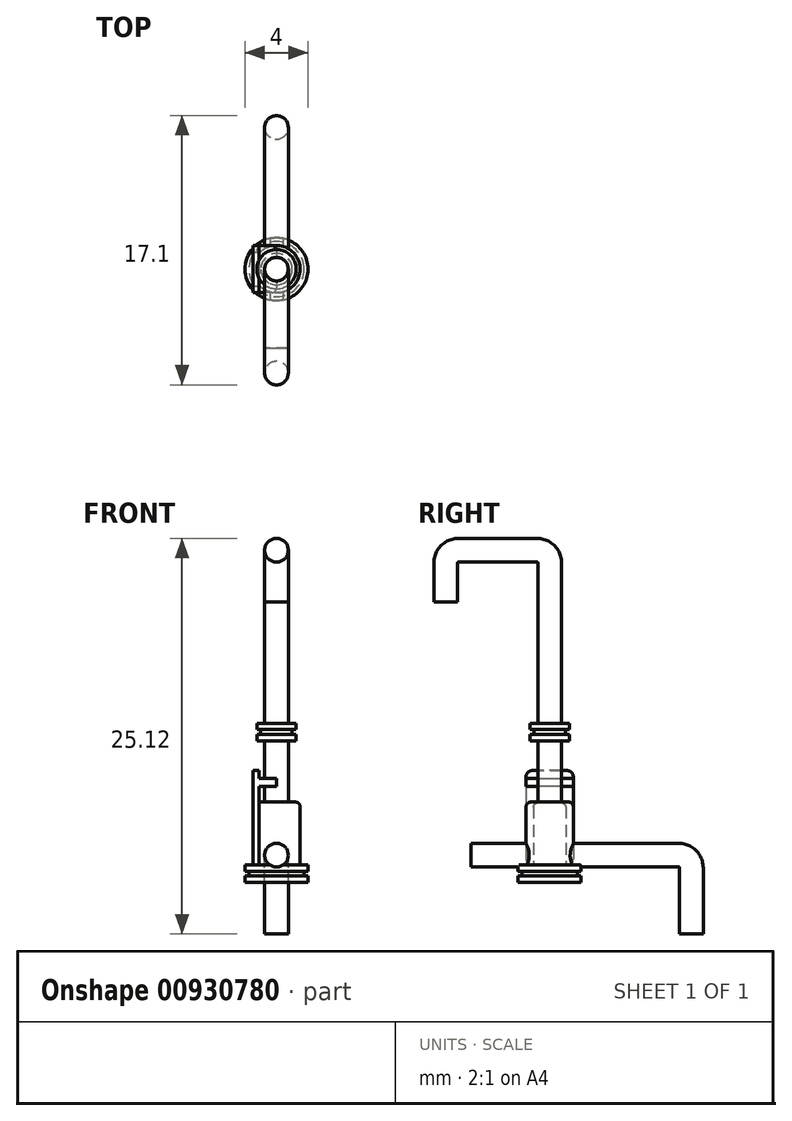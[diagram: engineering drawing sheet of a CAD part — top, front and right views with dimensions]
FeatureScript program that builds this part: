
annotation { "Feature Type Name" : "Feature", "Feature Type Description" : "" }
export const myFeature = defineFeature(function(context is Context, id is Id, definition is map)
    precondition{}
    {
        {
            var Q0;
            Q0=qCreatedBy(makeId("Right.planeOp"),FACE);
            var sketch = newSketch(context, id + "F0", { "sketchPlane" : qUnion([Q0])});
            skLineSegment(sketch, "E0", {"start": v(0, 0) * mm, "end": v(0, 2.5) * mm});
            skLineSegment(sketch, "E1", {"start": v(0.8, 3.3) * mm, "end": v(5.8, 3.3) * mm});
            skLineSegment(sketch, "E2", {"start": v(6.6, 2.5) * mm, "end": v(6.6, -16.7) * mm});
            skPoint(sketch, "E3.visualSharp", {"position": v(0, 3.3) * mm});
            skArc(sketch, "E3.filletArc", {"start": v(0.8, 3.3) * mm, "mid": v(0.23, 3.07) * mm, "end": v(0, 2.5) * mm});
            skPoint(sketch, "E4.visualSharp", {"position": v(6.6, 3.3) * mm});
            skArc(sketch, "E4.filletArc", {"start": v(6.6, 2.5) * mm, "mid": v(6.37, 3.07) * mm, "end": v(5.8, 3.3) * mm});
            skSolve(sketch);
        }
        {
            var Q0;
            Q0=qCreatedBy(makeId("Top.planeOp"),FACE);
            var sketch = newSketch(context, id + "F1", { "sketchPlane" : qUnion([Q0])});
            skCircle(sketch, "E5", {"center": v(0, 0) * mm, "radius": 0.75 * mm});
            skSolve(sketch);
        }
        {
            var Q0;
            Q0=makeQuery(id+"F1.imprint","IMPRINT",FACE,{"disambiguationData":[TD([[makeQuery(id+"F1.imprint","IMPRINT",EDGE,{"derivedFrom":sQuery(id+"F1.wireOp",EDGE,"E5")}),1.0]])]});
            var Q1;
            Q1=sQuery(id+"F0.wireOp",EDGE,"E1");
            var Q2;
            Q2=sQuery(id+"F0.wireOp",EDGE,"E0");
            var Q3;
            Q3=sQuery(id+"F0.wireOp",EDGE,"E3.filletArc");
            var Q4;
            Q4=sQuery(id+"F0.wireOp",EDGE,"E4.filletArc");
            var Q5;
            Q5=sQuery(id+"F0.wireOp",EDGE,"E2");
            sweep(context, id + "F2", {"profiles" : qUnion([Q0]), "path" : qUnion([Q1, Q2, Q3, Q4, Q5])});
        }
        {
            var Q0;
            Q0=makeQuery(id+"F2.opSweep","CAP_FACE",FACE,{"disambiguationData":[OSD([sQuery(id+"F0.wireOp",VERTEX,"E2.end"),sQuery(id+"F1.wireOp",EDGE,"E5")])],"isStart":false});
            var sketch = newSketch(context, id + "F3", { "sketchPlane" : qUnion([Q0])});
            skCircle(sketch, "E6", {"center": v(0, -6.6) * mm, "radius": 1.5 * mm});
            skSolve(sketch);
        }
        {
            var Q0;
            Q0=makeQuery(id+"F3.imprint","IMPRINT",FACE,{"disambiguationData":[TD([[makeQuery(id+"F3.imprint","IMPRINT",EDGE,{"derivedFrom":sQuery(id+"F3.wireOp",EDGE,"E6")}),1.0]])]});
            extrude(context, id + "F4", {"entities" : qUnion([Q0]), "operationType" : NewBodyOperationType.ADD, "oppositeDirection" : true, "depth" : 4 * mm, "offsetDistance" : 25 * mm});
        }
        {
            var Q0;
            {var subQ0=sQuery(id+"F1.wireOp",EDGE,"E5");var subQ1=sQuery(id+"F0.wireOp",VERTEX,"E2.end");Q0=makeQuery(id+"F4.boolean.opBoolean","MERGE",FACE,{"derivedFrom":[makeQuery(id+"F2.opSweep","CAP_FACE",FACE,{"disambiguationData":[OSD([subQ1,subQ0])],"isStart":false}),makeQuery(id+"F4.opExtrude","CAP_FACE",FACE,{"disambiguationData":[OSD([subQ1,subQ0,sQuery(id+"F3.wireOp",EDGE,"E6")])],"isStart":true})]});}
            var sketch = newSketch(context, id + "F5", { "sketchPlane" : qUnion([Q0])});
            skLineSegment(sketch, "E7", {"start": v(0, -6.6) * mm, "end": v(-2.5, -6.6) * mm, "construction": true});
            skLineSegment(sketch, "E8", {"start": v(-1.5, -6.6) * mm, "end": v(-1.5, -8.1) * mm});
            skLineSegment(sketch, "E9", {"start": v(-1.5, -8.1) * mm, "end": v(-1.1, -8.1) * mm});
            skLineSegment(sketch, "E10", {"start": v(-1.1, -8.1) * mm, "end": v(-1.1, -5.1) * mm});
            skLineSegment(sketch, "E11", {"start": v(-1.1, -5.1) * mm, "end": v(-1.5, -5.1) * mm});
            skLineSegment(sketch, "E12", {"start": v(-1.5, -5.1) * mm, "end": v(-1.5, -6.6) * mm});
            skSolve(sketch);
        }
        {
            var Q0;
            {var subQ0=sQuery(id+"F5.wireOp",EDGE,"E8");Q0=makeQuery(id+"F5.imprint","IMPRINT",FACE,{"disambiguationData":[TD([[makeQuery(id+"F5.imprint","IMPRINT",EDGE,{"derivedFrom":subQ0}),1.0]])]});}
            var Q1;
            {var subQ0=sQuery(id+"F5.wireOp",EDGE,"E11");Q1=makeQuery(id+"F5.imprint","IMPRINT",FACE,{"disambiguationData":[TD([[makeQuery(id+"F5.imprint","IMPRINT",EDGE,{"derivedFrom":subQ0}),1.0]])]});}
            var Q2;
            {var subQ0=sQuery(id+"F5.wireOp",EDGE,"E10");var subQ1=makeQuery(id+"F4.opExtrude","CAP_EDGE",EDGE,{"disambiguationData":[OSD([sQuery(id+"F3.wireOp",EDGE,"E6")])],"isStart":true});var subQ2=makeQuery(id+"F5.imprint","INTERSECT",VERTEX,{"disambiguationData":[OD(0.0)],"derivedFrom":[subQ1,subQ0]});Q2=makeQuery(id+"F5.imprint","IMPRINT",FACE,{"disambiguationData":[TD([[makeQuery(id+"F5.imprint","IMPRINT",EDGE,{"disambiguationData":[TD([[subQ2,-1.0]])],"derivedFrom":subQ0}),1.0]])]});}
            extrude(context, id + "F6", {"entities" : qUnion([Q0, Q1, Q2]), "operationType" : NewBodyOperationType.ADD, "oppositeDirection" : true, "depth" : 6 * mm, "offsetDistance" : 25 * mm});
        }
        {
            var Q0;
            Q0=makeQuery(id+"F6.opExtrude","CAP_EDGE",EDGE,{"disambiguationData":[OSD([sQuery(id+"F5.wireOp",EDGE,"E9")])],"isStart":false});
            var Q1;
            Q1=makeQuery(id+"F6.opExtrude","CAP_EDGE",EDGE,{"disambiguationData":[OSD([sQuery(id+"F5.wireOp",EDGE,"E11")])],"isStart":false});
            var Q2;
            Q2=makeQuery(id+"F6.opExtrude","CAP_EDGE",EDGE,{"disambiguationData":[OSD([sQuery(id+"F5.wireOp",EDGE,"E9")])],"isStart":true});
            var Q3;
            Q3=makeQuery(id+"F6.opExtrude","CAP_EDGE",EDGE,{"disambiguationData":[OSD([sQuery(id+"F5.wireOp",EDGE,"E11")])],"isStart":true});
            fillet(context, id + "F7", {"entities" : qUnion([Q0, Q1, Q2, Q3]), "radius" : 0.4 * mm, "tangentPropagation" : true, "allowEdgeOverflow" : false});
        }
        {
            var Q0;
            {var subQ0=sQuery(id+"F1.wireOp",EDGE,"E5");var subQ1=sQuery(id+"F0.wireOp",VERTEX,"E2.end");Q0=makeQuery(id+"F6.boolean.opBoolean","MERGE",FACE,{"derivedFrom":[makeQuery(id+"F4.boolean.opBoolean","MERGE",FACE,{"derivedFrom":[makeQuery(id+"F2.opSweep","CAP_FACE",FACE,{"disambiguationData":[OSD([subQ1,subQ0])],"isStart":false}),makeQuery(id+"F4.opExtrude","CAP_FACE",FACE,{"disambiguationData":[OSD([subQ1,subQ0,sQuery(id+"F3.wireOp",EDGE,"E6")])],"isStart":true})]}),makeQuery(id+"F6.opExtrude","CAP_FACE",FACE,{"disambiguationData":[OSD([sQuery(id+"F5.wireOp",EDGE,"E8"),sQuery(id+"F5.wireOp",EDGE,"E9"),sQuery(id+"F5.wireOp",EDGE,"E10"),sQuery(id+"F5.wireOp",EDGE,"E11"),sQuery(id+"F5.wireOp",EDGE,"E12")])],"isStart":true})]});}
            var sketch = newSketch(context, id + "F8", { "sketchPlane" : qUnion([Q0])});
            skCircle(sketch, "E13", {"center": v(0, -6.6) * mm, "radius": 2 * mm});
            skSolve(sketch);
        }
        {
            var Q0;
            Q0=makeQuery(id+"F8.imprint","IMPRINT",FACE,{"disambiguationData":[TD([[makeQuery(id+"F8.imprint","IMPRINT",EDGE,{"derivedFrom":sQuery(id+"F8.wireOp",EDGE,"E13")}),1.0]])]});
            var Q1;
            {var subQ6=sQuery(id+"F3.wireOp",EDGE,"E6");Q1=makeQuery(id+"F8.imprint","IMPRINT",FACE,{"disambiguationData":[TD([[makeQuery(id+"F8.imprint","IMPRINT",EDGE,{"derivedFrom":makeQuery(id+"F4.opExtrude","CAP_EDGE",EDGE,{"disambiguationData":[OSD([subQ6])],"isStart":true})}),1.0]])]});}
            extrude(context, id + "F9", {"entities" : qUnion([Q0, Q1]), "operationType" : NewBodyOperationType.ADD, "depth" : 0.4 * mm, "offsetDistance" : 25 * mm});
        }
        {
            var Q0;
            Q0=makeQuery(id+"F9.opExtrude","CAP_FACE",FACE,{"disambiguationData":[OSD([sQuery(id+"F8.wireOp",EDGE,"E13")])],"isStart":false});
            var sketch = newSketch(context, id + "F10", { "sketchPlane" : qUnion([Q0])});
            skCircle(sketch, "E14", {"center": v(0, -6.6) * mm, "radius": 1.75 * mm});
            skSolve(sketch);
        }
        {
            var Q0;
            Q0=makeQuery(id+"F10.imprint","IMPRINT",FACE,{"disambiguationData":[TD([[makeQuery(id+"F10.imprint","IMPRINT",EDGE,{"derivedFrom":sQuery(id+"F10.wireOp",EDGE,"E14")}),1.0]])]});
            extrude(context, id + "F11", {"entities" : qUnion([Q0]), "operationType" : NewBodyOperationType.ADD, "depth" : 0.3 * mm, "offsetDistance" : 25 * mm});
        }
        {
            var Q0;
            Q0=makeQuery(id+"F11.opExtrude","CAP_FACE",FACE,{"disambiguationData":[OSD([sQuery(id+"F10.wireOp",EDGE,"E14")])],"isStart":false});
            var sketch = newSketch(context, id + "F12", { "sketchPlane" : qUnion([Q0])});
            skCircle(sketch, "E15", {"center": v(0, -6.6) * mm, "radius": 2 * mm});
            skSolve(sketch);
        }
        {
            var Q0;
            Q0=makeQuery(id+"F12.imprint","IMPRINT",FACE,{"disambiguationData":[TD([[makeQuery(id+"F12.imprint","IMPRINT",EDGE,{"derivedFrom":sQuery(id+"F12.wireOp",EDGE,"E15")}),1.0]])]});
            var Q1;
            Q1=makeQuery(id+"F12.imprint","IMPRINT",FACE,{"disambiguationData":[TD([[makeQuery(id+"F12.imprint","IMPRINT",EDGE,{"derivedFrom":makeQuery(id+"F11.opExtrude","CAP_EDGE",EDGE,{"disambiguationData":[OSD([sQuery(id+"F10.wireOp",EDGE,"E14")])],"isStart":false})}),1.0]])]});
            extrude(context, id + "F13", {"entities" : qUnion([Q0, Q1]), "operationType" : NewBodyOperationType.ADD, "depth" : 0.4 * mm, "offsetDistance" : 25 * mm});
        }
        {
            var Q0;
            Q0=makeQuery(id+"F6.opExtrude","SWEPT_FACE",FACE,{"disambiguationData":[OSD([sQuery(id+"F5.wireOp",EDGE,"E8"),sQuery(id+"F5.wireOp",EDGE,"E12")])]});
            var sketch = newSketch(context, id + "F14", { "sketchPlane" : qUnion([Q0])});
            skLineSegment(sketch, "E16", {"start": v(-8.1, -11.2) * mm, "end": v(-5.1, -11.2) * mm});
            skLineSegment(sketch, "E17", {"start": v(-5.1, -11.2) * mm, "end": v(-5.1, -11.7) * mm});
            skLineSegment(sketch, "E18", {"start": v(-5.1, -11.7) * mm, "end": v(-8.1, -11.7) * mm});
            skLineSegment(sketch, "E19", {"start": v(-8.1, -11.2) * mm, "end": v(-8.1, -11.7) * mm});
            skSolve(sketch);
        }
        {
            var Q0;
            Q0=makeQuery(id+"F14.imprint","IMPRINT",FACE,{"disambiguationData":[TD([[makeQuery(id+"F14.imprint","IMPRINT",EDGE,{"derivedFrom":sQuery(id+"F14.wireOp",EDGE,"E16")}),-1.0]])]});
            var Q1;
            Q1=qCreatedBy(makeId("Right.planeOp"),FACE);
            extrude(context, id + "F15", {"entities" : qUnion([Q0]), "operationType" : NewBodyOperationType.ADD, "endBound" : BoundingType.UP_TO_SURFACE, "oppositeDirection" : true, "depth" : 25 * mm, "endBoundEntityFace" : qUnion([Q1]), "offsetDistance" : 25 * mm});
        }
        {
            var Q0;
            Q0=makeQuery(id+"F15.opExtrude","CAP_EDGE",EDGE,{"disambiguationData":[OSD([sQuery(id+"F14.wireOp",EDGE,"E19")])],"isStart":false});
            var Q1;
            Q1=makeQuery(id+"F15.opExtrude","CAP_EDGE",EDGE,{"disambiguationData":[OSD([sQuery(id+"F14.wireOp",EDGE,"E17")])],"isStart":false});
            fillet(context, id + "F16", {"entities" : qUnion([Q0, Q1]), "radius" : 0.3 * mm, "tangentPropagation" : true, "allowEdgeOverflow" : false});
        }
        {
            var Q0;
            Q0=makeQuery(id+"F13.opExtrude","CAP_FACE",FACE,{"disambiguationData":[OSD([sQuery(id+"F12.wireOp",EDGE,"E15")])],"isStart":false});
            cPlane(context, id + "F17", {"entities" : qUnion([Q0]), "cplaneType" : CPlaneType.OFFSET, "offset" : 9 * mm, "oppositeDirection" : true, "width" : 150 * mm, "height" : 150 * mm});
        }
        {
            var Q0;
            Q0=qCreatedBy(id+"F17.planeOp",FACE);
            var sketch = newSketch(context, id + "F18", { "sketchPlane" : qUnion([Q0])});
            skCircle(sketch, "E20.0", {"center": v(0, -6.6) * mm, "radius": 0.75 * mm});
            skCircle(sketch, "E21", {"center": v(0, -6.6) * mm, "radius": 1.25 * mm});
            skSolve(sketch);
        }
        {
            var Q0;
            Q0=makeQuery(id+"F18.imprint","IMPRINT",FACE,{"disambiguationData":[TD([[makeQuery(id+"F18.imprint","IMPRINT",EDGE,{"derivedFrom":sQuery(id+"F18.wireOp",EDGE,"E20.0")}),-1.0]])]});
            extrude(context, id + "F19", {"entities" : qUnion([Q0]), "operationType" : NewBodyOperationType.ADD, "oppositeDirection" : true, "depth" : 0.4 * mm, "offsetDistance" : 25 * mm});
        }
        {
            var Q0;
            Q0=makeQuery(id+"F19.opExtrude","CAP_FACE",FACE,{"disambiguationData":[OSD([sQuery(id+"F18.wireOp",EDGE,"E20.0"),sQuery(id+"F18.wireOp",EDGE,"E21")])],"isStart":false});
            var sketch = newSketch(context, id + "F20", { "sketchPlane" : qUnion([Q0])});
            skCircle(sketch, "E22", {"center": v(0, 6.6) * mm, "radius": 1 * mm});
            skSolve(sketch);
        }
        {
            var Q0;
            Q0=makeQuery(id+"F20.imprint","IMPRINT",FACE,{"disambiguationData":[TD([[makeQuery(id+"F20.imprint","IMPRINT",EDGE,{"derivedFrom":sQuery(id+"F20.wireOp",EDGE,"E22")}),1.0]])]});
            extrude(context, id + "F21", {"entities" : qUnion([Q0]), "operationType" : NewBodyOperationType.ADD, "depth" : 0.3 * mm, "offsetDistance" : 25 * mm});
        }
        {
            var Q0;
            Q0=makeQuery(id+"F21.opExtrude","CAP_FACE",FACE,{"disambiguationData":[OSD([sQuery(id+"F18.wireOp",EDGE,"E20.0"),sQuery(id+"F20.wireOp",EDGE,"E22")])],"isStart":false});
            var sketch = newSketch(context, id + "F22", { "sketchPlane" : qUnion([Q0])});
            skCircle(sketch, "E23", {"center": v(0, 6.6) * mm, "radius": 1.25 * mm});
            skSolve(sketch);
        }
        {
            var Q0;
            Q0=makeQuery(id+"F22.imprint","IMPRINT",FACE,{"disambiguationData":[TD([[makeQuery(id+"F22.imprint","IMPRINT",EDGE,{"derivedFrom":sQuery(id+"F22.wireOp",EDGE,"E23")}),1.0]])]});
            var Q1;
            Q1=makeQuery(id+"F22.imprint","IMPRINT",FACE,{"disambiguationData":[TD([[makeQuery(id+"F22.imprint","IMPRINT",EDGE,{"derivedFrom":makeQuery(id+"F21.opExtrude","CAP_EDGE",EDGE,{"disambiguationData":[OSD([sQuery(id+"F20.wireOp",EDGE,"E22")])],"isStart":false})}),1.0]])]});
            extrude(context, id + "F23", {"entities" : qUnion([Q0, Q1]), "operationType" : NewBodyOperationType.ADD, "depth" : 0.4 * mm, "offsetDistance" : 25 * mm});
        }
        {
            var Q0;
            Q0=makeQuery(id+"F4.opExtrude","CAP_EDGE",EDGE,{"disambiguationData":[OSD([sQuery(id+"F3.wireOp",EDGE,"E6")])],"isStart":false});
            fillet(context, id + "F24", {"entities" : qUnion([Q0]), "radius" : 0.3 * mm, "tangentPropagation" : true, "allowEdgeOverflow" : false});
        }
        {
            var Q0;
            Q0=makeQuery(id+"F6.opExtrude","CAP_EDGE",EDGE,{"disambiguationData":[OSD([sQuery(id+"F5.wireOp",EDGE,"E8"),sQuery(id+"F5.wireOp",EDGE,"E12")])],"isStart":false});
            cPoint(context, id + "F25", {"entities" : qUnion([Q0]), "parameter" : 0.5});
        }
        {
            var Q0;
            Q0=qCreatedBy(makeId("Front.planeOp"),FACE);
            var Q1;
            Q1 = qCreatedBy(id + "F25" ,VERTEX);
            cPlane(context, id + "F26", {"entities" : qUnion([Q0, Q1]), "cplaneType" : CPlaneType.PLANE_POINT, "offset" : 25 * mm, "oppositeDirection" : true, "width" : 150 * mm, "height" : 150 * mm});
        }
        {
            var Q0;
            Q0=qCreatedBy(id+"F26.planeOp",FACE);
            var sketch = newSketch(context, id + "F27", { "sketchPlane" : qUnion([Q0])});
            skCircle(sketch, "E24", {"center": v(0, -16.07) * mm, "radius": 0.75 * mm});
            skSolve(sketch);
        }
        {
            var Q0;
            Q0=qCreatedBy(makeId("Right.planeOp"),FACE);
            var sketch = newSketch(context, id + "F28", { "sketchPlane" : qUnion([Q0])});
            skPoint(sketch, "E25.0", {"position": v(6.6, -16.07) * mm});
            skLineSegment(sketch, "E26", {"start": v(6.6, -16.07) * mm, "end": v(1.6, -16.07) * mm});
            skLineSegment(sketch, "E27", {"start": v(6.6, -16.07) * mm, "end": v(14.8, -16.07) * mm});
            skLineSegment(sketch, "E28", {"start": v(15.6, -16.87) * mm, "end": v(15.6, -21.07) * mm});
            skPoint(sketch, "E29.visualSharp", {"position": v(15.6, -16.07) * mm});
            skArc(sketch, "E29.filletArc", {"start": v(15.6, -16.87) * mm, "mid": v(15.37, -16.3) * mm, "end": v(14.8, -16.07) * mm});
            skSolve(sketch);
        }
        {
            var Q0;
            Q0 = qSketchRegion(id + "F27", true);
            var Q1;
            Q1=sQuery(id+"F28.wireOp",EDGE,"E26");
            var Q2;
            Q2=sQuery(id+"F28.wireOp",EDGE,"E27");
            var Q3;
            Q3=sQuery(id+"F28.wireOp",EDGE,"E29.filletArc");
            var Q4;
            Q4=sQuery(id+"F28.wireOp",EDGE,"E28");
            sweep(context, id + "F29", {"operationType" : NewBodyOperationType.ADD, "profiles" : qUnion([Q0]), "path" : qUnion([Q1, Q2, Q3, Q4])});
        }
    });
